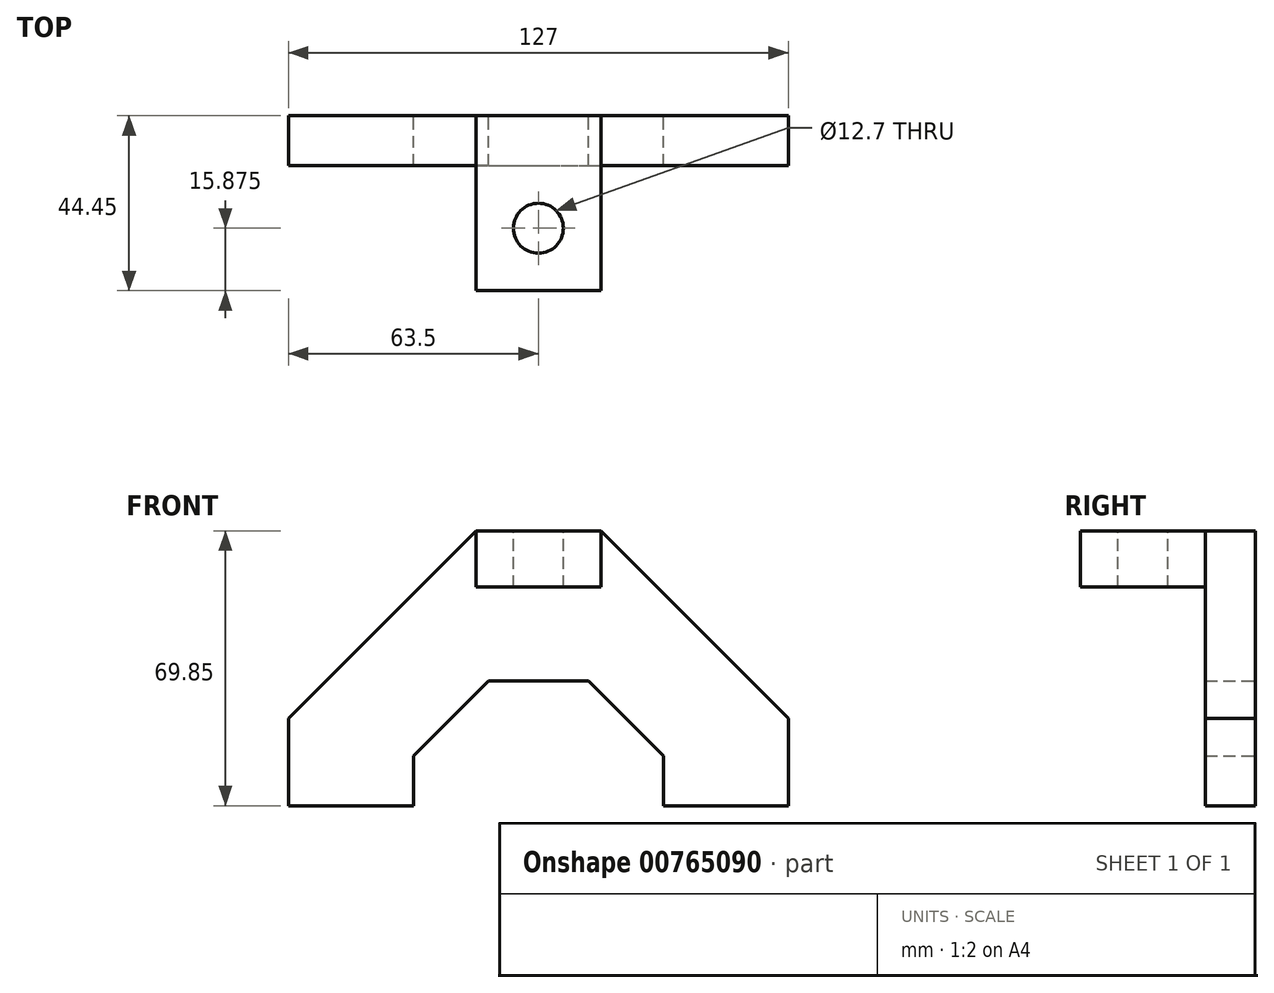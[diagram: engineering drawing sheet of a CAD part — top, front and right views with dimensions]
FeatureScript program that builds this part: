
annotation { "Feature Type Name" : "Feature", "Feature Type Description" : "" }
export const myFeature = defineFeature(function(context is Context, id is Id, definition is map)
    precondition{}
    {
        {
            var Q0;
            Q0=qCreatedBy(makeId("Front.planeOp"),FACE);
            var sketch = newSketch(context, id + "F0", { "sketchPlane" : qUnion([Q0])});
            skLineSegment(sketch, "E0", {"start": v(-60.1, -35.62) * mm, "end": v(-60.1, -13.4) * mm});
            skLineSegment(sketch, "E1", {"start": v(-60.1, -35.62) * mm, "end": v(66.9, -35.62) * mm});
            skLineSegment(sketch, "E2", {"start": v(66.9, -35.62) * mm, "end": v(66.9, -13.4) * mm});
            skLineSegment(sketch, "E3", {"start": v(-60.1, -35.62) * mm, "end": v(-28.36, -35.62) * mm});
            skLineSegment(sketch, "E4", {"start": v(-28.36, -35.62) * mm, "end": v(35.14, -35.62) * mm});
            skLineSegment(sketch, "E5", {"start": v(35.14, -35.62) * mm, "end": v(66.9, -35.62) * mm});
            skLineSegment(sketch, "E6", {"start": v(-28.36, -35.62) * mm, "end": v(-28.36, -22.92) * mm});
            skLineSegment(sketch, "E7", {"start": v(35.14, -35.62) * mm, "end": v(35.14, -22.92) * mm});
            skLineSegment(sketch, "E8", {"start": v(-9.3, -3.87) * mm, "end": v(16.1, -3.87) * mm});
            skLineSegment(sketch, "E9", {"start": v(-9.3, -3.87) * mm, "end": v(-28.36, -22.92) * mm});
            skLineSegment(sketch, "E10", {"start": v(16.1, -3.87) * mm, "end": v(35.14, -22.92) * mm});
            skLineSegment(sketch, "E11", {"start": v(-60.1, -35.62) * mm, "end": v(-12.48, -35.62) * mm});
            skLineSegment(sketch, "E12", {"start": v(66.9, -35.62) * mm, "end": v(19.27, -35.62) * mm});
            skLineSegment(sketch, "E13", {"start": v(19.27, 34.23) * mm, "end": v(-12.48, 34.23) * mm});
            skLineSegment(sketch, "E14", {"start": v(-60.1, -13.4) * mm, "end": v(-12.48, 34.23) * mm});
            skLineSegment(sketch, "E15", {"start": v(19.27, 34.23) * mm, "end": v(66.9, -13.4) * mm});
            skLineSegment(sketch, "E16", {"start": v(-12.48, 34.23) * mm, "end": v(-12.48, 19.95) * mm});
            skLineSegment(sketch, "E17", {"start": v(-12.48, 19.95) * mm, "end": v(19.27, 19.95) * mm});
            skLineSegment(sketch, "E18", {"start": v(19.27, 19.95) * mm, "end": v(19.27, 34.23) * mm});
            skSolve(sketch);
        }
        {
            var Q0;
            {var subQ4=sQuery(id+"F0.wireOp",EDGE,"E0");Q0=makeQuery(id+"F0.imprint","IMPRINT",FACE,{"disambiguationData":[TD([[makeQuery(id+"F0.imprint","IMPRINT",EDGE,{"derivedFrom":subQ4}),-1.0]])]});}
            extrude(context, id + "F1", {"entities" : qUnion([Q0]), "depth" : 12.7 * mm, "offsetDistance" : 25.4 * mm});
        }
        {
            var Q0;
            {var subQ2=sQuery(id+"F0.wireOp",EDGE,"E4");Q0=makeQuery(id+"F0.imprint","IMPRINT",FACE,{"disambiguationData":[TD([[makeQuery(id+"F0.imprint","IMPRINT",EDGE,{"derivedFrom":subQ2}),1.0]])]});}
            var Q1;
            Q1=makeQuery(id+"F0.imprint","IMPRINT",FACE,{"disambiguationData":[TD([[makeQuery(id+"F0.imprint","IMPRINT",EDGE,{"derivedFrom":sQuery(id+"F0.wireOp",EDGE,"E13")}),1.0]])]});
            extrude(context, id + "F2", {"entities" : qUnion([Q0, Q1]), "operationType" : NewBodyOperationType.ADD, "depth" : 44.45 * mm, "offsetDistance" : 25.4 * mm});
        }
        {
            var Q0;
            Q0=makeQuery(id+"F2.opExtrude","SWEPT_FACE",FACE,{"disambiguationData":[OSD([sQuery(id+"F0.wireOp",EDGE,"E13")])]});
            var sketch = newSketch(context, id + "F3", { "sketchPlane" : qUnion([Q0])});
            skCircle(sketch, "E19", {"center": v(3.4, -28.58) * mm, "radius": 6.35 * mm});
            skSolve(sketch);
        }
        {
            var Q0;
            Q0 = qSketchRegion(id + "F3", true);
            extrude(context, id + "F4", {"entities" : qUnion([Q0]), "operationType" : NewBodyOperationType.REMOVE, "oppositeDirection" : true, "depth" : 25.4 * mm, "offsetDistance" : 25.4 * mm});
        }
    });
